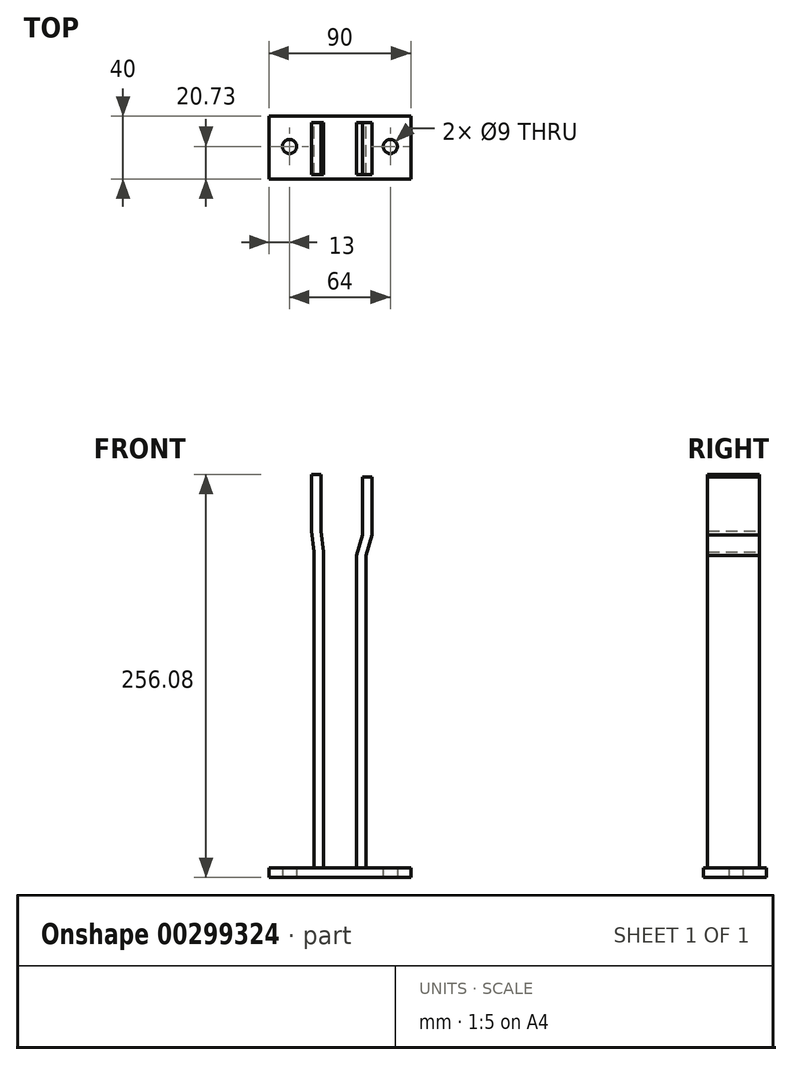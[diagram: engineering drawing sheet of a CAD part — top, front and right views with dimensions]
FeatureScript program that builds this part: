
annotation { "Feature Type Name" : "Feature", "Feature Type Description" : "" }
export const myFeature = defineFeature(function(context is Context, id is Id, definition is map)
    precondition{}
    {
        {
            var Q0;
            Q0=qCreatedBy(makeId("Right.planeOp"),FACE);
            var sketch = newSketch(context, id + "F0", { "sketchPlane" : qUnion([Q0])});
            skLineSegment(sketch, "E0.bottom", {"start": v(-20.73, 6) * mm, "end": v(19.27, 6) * mm});
            skLineSegment(sketch, "E0.left", {"start": v(-20.73, 6) * mm, "end": v(-20.73, 0) * mm});
            skLineSegment(sketch, "E0.right", {"start": v(19.27, 6) * mm, "end": v(19.27, 0) * mm});
            skLineSegment(sketch, "E1.trimOffspring", {"start": v(-20.73, 0) * mm, "end": v(19.27, 0) * mm});
            skSolve(sketch);
        }
        {
            var Q0;
            {var subQ3=sQuery(id+"F0.wireOp",EDGE,"ff7b447e-6627-4066-b775-27bb9192647b.left");Q0=makeQuery(id+"F0.imprint","IMPRINT",FACE,{"disambiguationData":[TD([[makeQuery(id+"F0.imprint","IMPRINT",EDGE,{"derivedFrom":subQ3}),-1.0]])]});}
            var Q1;
            {var subQ3=sQuery(id+"F0.wireOp",EDGE,"ff7b447e-6627-4066-b775-27bb9192647b.right");Q1=makeQuery(id+"F0.imprint","IMPRINT",FACE,{"disambiguationData":[TD([[makeQuery(id+"F0.imprint","IMPRINT",EDGE,{"derivedFrom":subQ3}),1.0]])]});}
            var Q2;
            {var subQ0=sQuery(id+"F0.wireOp",EDGE,"ff7b447e-6627-4066-b775-27bb9192647b.top");Q2=makeQuery(id+"F0.imprint","IMPRINT",FACE,{"disambiguationData":[TD([[makeQuery(id+"F0.imprint","IMPRINT",EDGE,{"derivedFrom":subQ0}),-1.0]])]});}
            var Q3;
            {var subQ5=sQuery(id+"F0.wireOp",EDGE,"E0.left");Q3=makeQuery(id+"F0.imprint","IMPRINT",FACE,{"disambiguationData":[TD([[makeQuery(id+"F0.imprint","IMPRINT",EDGE,{"derivedFrom":subQ5}),1.0]])]});}
            var Q4;
            {var subQ5=sQuery(id+"F0.wireOp",EDGE,"E0.right");Q4=makeQuery(id+"F0.imprint","IMPRINT",FACE,{"disambiguationData":[TD([[makeQuery(id+"F0.imprint","IMPRINT",EDGE,{"derivedFrom":subQ5}),-1.0]])]});}
            extrude(context, id + "F1", {"entities" : qUnion([Q0, Q1, Q2, Q3, Q4]), "depth" : 90 * mm});
        }
        {
            var Q0;
            Q0=qCreatedBy(makeId("Top.planeOp"),FACE);
            var sketch = newSketch(context, id + "F2", { "sketchPlane" : qUnion([Q0])});
            skLineSegment(sketch, "E2.bottom", {"start": v(28.5, 14.5) * mm, "end": v(34.5, 14.5) * mm});
            skLineSegment(sketch, "E2.top", {"start": v(28.5, -15.98) * mm, "end": v(34.5, -15.98) * mm});
            skLineSegment(sketch, "E2.left", {"start": v(28.5, 14.5) * mm, "end": v(28.5, -15.98) * mm});
            skLineSegment(sketch, "E2.right", {"start": v(34.5, 14.5) * mm, "end": v(34.5, -15.98) * mm});
            skLineSegment(sketch, "E3.bottom", {"start": v(55.5, 14.27) * mm, "end": v(61.5, 14.27) * mm});
            skLineSegment(sketch, "E3.top", {"start": v(55.5, -15.73) * mm, "end": v(61.5, -15.73) * mm});
            skLineSegment(sketch, "E3.left", {"start": v(55.5, 14.27) * mm, "end": v(55.5, -15.73) * mm});
            skLineSegment(sketch, "E3.right", {"start": v(61.5, 14.27) * mm, "end": v(61.5, -15.73) * mm});
            skLineSegment(sketch, "E4", {"start": v(0, -20.73) * mm, "end": v(90, -20.73) * mm, "construction": true});
            skLineSegment(sketch, "E5", {"start": v(90, 19.27) * mm, "end": v(90, -20.73) * mm, "construction": true});
            skPoint(sketch, "E6.center.orphan", {"position": v(77, 0) * mm});
            skPoint(sketch, "E7.center.orphan", {"position": v(13, 0) * mm});
            skSolve(sketch);
        }
        {
            var Q0;
            Q0=qCreatedBy(makeId("Top.planeOp"),FACE);
            var sketch = newSketch(context, id + "F3", { "sketchPlane" : qUnion([Q0])});
            skCircle(sketch, "E8", {"center": v(77, 0) * mm, "radius": 5 * mm});
            skCircle(sketch, "E9", {"center": v(13, 0) * mm, "radius": 5 * mm});
            skSolve(sketch);
        }
        {
            var Q0;
            Q0=sQuery(id+"F3.wireOp",VERTEX,"E9.center");
            var Q1;
            Q1=sQuery(id+"F3.wireOp",VERTEX,"E8.center");
            var Q2;
            Q2=makeQuery(id+"F1.opExtrude","SWEPT_BODY",BODY,{"disambiguationData":[OSD([sQuery(id+"F0.wireOp",EDGE,"E0.bottom"),sQuery(id+"F0.wireOp",EDGE,"E0.left"),sQuery(id+"F0.wireOp",EDGE,"E0.right"),sQuery(id+"F0.wireOp",EDGE,"E1.trimOffspring")])]});
            hole(context, id + "F4", {"style" : HoleStyle.SIMPLE, "endStyle" : HoleEndStyle.THROUGH, "oppositeDirection" : true, "holeDiameter" : 9 * mm, "tappedDepth" : 12 * mm, "tapClearance" : 3, "locations" : qUnion([Q0, Q1]), "scope" : qUnion([Q2])});
        }
        {
            var Q0;
            Q0=qCreatedBy(makeId("Front.planeOp"),FACE);
            var sketch = newSketch(context, id + "F5", { "sketchPlane" : qUnion([Q0])});
            skLineSegment(sketch, "E10.bottom", {"start": v(28.5, 206.79) * mm, "end": v(34.5, 206.79) * mm});
            skLineSegment(sketch, "E10.top", {"start": v(28.5, 0) * mm, "end": v(34.5, 0) * mm});
            skLineSegment(sketch, "E10.left", {"start": v(28.5, 206.79) * mm, "end": v(28.5, 0) * mm});
            skLineSegment(sketch, "E10.right", {"start": v(34.5, 206.79) * mm, "end": v(34.5, 0) * mm});
            skLineSegment(sketch, "E11.bottom", {"start": v(55.5, 204.63) * mm, "end": v(61.5, 204.63) * mm});
            skLineSegment(sketch, "E11.top", {"start": v(55.5, 0) * mm, "end": v(61.5, 0) * mm});
            skLineSegment(sketch, "E11.left", {"start": v(55.5, 204.63) * mm, "end": v(55.5, 0) * mm});
            skLineSegment(sketch, "E11.right", {"start": v(61.5, 204.63) * mm, "end": v(61.5, 0) * mm});
            skLineSegment(sketch, "E12.bottom", {"start": v(59.42, 217.5) * mm, "end": v(65.42, 217.5) * mm});
            skLineSegment(sketch, "E12.top", {"start": v(59.42, 254.49) * mm, "end": v(65.42, 254.49) * mm});
            skLineSegment(sketch, "E12.left", {"start": v(59.42, 217.5) * mm, "end": v(59.42, 254.49) * mm});
            skLineSegment(sketch, "E12.right", {"start": v(65.42, 217.5) * mm, "end": v(65.42, 254.49) * mm});
            skLineSegment(sketch, "E13.bottom", {"start": v(32.97, 219.9) * mm, "end": v(26.97, 219.9) * mm});
            skLineSegment(sketch, "E13.top", {"start": v(32.97, 256.08) * mm, "end": v(26.97, 256.08) * mm});
            skLineSegment(sketch, "E13.left", {"start": v(32.97, 219.9) * mm, "end": v(32.97, 256.08) * mm});
            skLineSegment(sketch, "E13.right", {"start": v(26.97, 219.9) * mm, "end": v(26.97, 256.08) * mm});
            skLineSegment(sketch, "E14", {"start": v(26.97, 219.9) * mm, "end": v(28.5, 206.79) * mm});
            skLineSegment(sketch, "E15", {"start": v(32.97, 219.9) * mm, "end": v(34.5, 206.79) * mm});
            skLineSegment(sketch, "E16", {"start": v(59.42, 217.5) * mm, "end": v(55.5, 204.63) * mm});
            skLineSegment(sketch, "E17", {"start": v(65.42, 217.5) * mm, "end": v(61.5, 204.63) * mm});
            skSolve(sketch);
        }
        {
            var Q0;
            Q0=makeQuery(id+"F5.imprint","IMPRINT",FACE,{"disambiguationData":[TD([[makeQuery(id+"F5.imprint","IMPRINT",EDGE,{"derivedFrom":sQuery(id+"F5.wireOp",EDGE,"E12.bottom")}),1.0]])]});
            var Q1;
            Q1=makeQuery(id+"F5.imprint","IMPRINT",FACE,{"disambiguationData":[TD([[makeQuery(id+"F5.imprint","IMPRINT",EDGE,{"derivedFrom":sQuery(id+"F5.wireOp",EDGE,"E11.bottom")}),1.0]])]});
            var Q2;
            Q2=makeQuery(id+"F5.imprint","IMPRINT",FACE,{"disambiguationData":[TD([[makeQuery(id+"F5.imprint","IMPRINT",EDGE,{"derivedFrom":sQuery(id+"F5.wireOp",EDGE,"E11.bottom")}),-1.0]])]});
            var Q3;
            Q3=makeQuery(id+"F5.imprint","IMPRINT",FACE,{"disambiguationData":[TD([[makeQuery(id+"F5.imprint","IMPRINT",EDGE,{"derivedFrom":sQuery(id+"F5.wireOp",EDGE,"E10.bottom")}),-1.0]])]});
            var Q4;
            Q4=makeQuery(id+"F5.imprint","IMPRINT",FACE,{"disambiguationData":[TD([[makeQuery(id+"F5.imprint","IMPRINT",EDGE,{"derivedFrom":sQuery(id+"F5.wireOp",EDGE,"E10.bottom")}),1.0]])]});
            var Q5;
            Q5=makeQuery(id+"F5.imprint","IMPRINT",FACE,{"disambiguationData":[TD([[makeQuery(id+"F5.imprint","IMPRINT",EDGE,{"derivedFrom":sQuery(id+"F5.wireOp",EDGE,"E13.bottom")}),-1.0]])]});
            extrude(context, id + "F6", {"entities" : qUnion([Q0, Q1, Q2, Q3, Q4, Q5]), "operationType" : NewBodyOperationType.ADD, "depth" : 18 * mm});
        }
        {
            var Q0;
            Q0=makeQuery(id+"F6.opExtrude","CAP_FACE",FACE,{"disambiguationData":[OSD([sQuery(id+"F5.wireOp",EDGE,"E10.top"),sQuery(id+"F5.wireOp",EDGE,"E10.left"),sQuery(id+"F5.wireOp",EDGE,"E10.right"),sQuery(id+"F5.wireOp",EDGE,"E13.top"),sQuery(id+"F5.wireOp",EDGE,"E13.left"),sQuery(id+"F5.wireOp",EDGE,"E13.right"),sQuery(id+"F5.wireOp",EDGE,"E14"),sQuery(id+"F5.wireOp",EDGE,"E15")])],"isStart":true});
            var Q1;
            Q1=makeQuery(id+"F6.opExtrude","CAP_FACE",FACE,{"disambiguationData":[OSD([sQuery(id+"F5.wireOp",EDGE,"E11.top"),sQuery(id+"F5.wireOp",EDGE,"E11.left"),sQuery(id+"F5.wireOp",EDGE,"E11.right"),sQuery(id+"F5.wireOp",EDGE,"E12.top"),sQuery(id+"F5.wireOp",EDGE,"E12.left"),sQuery(id+"F5.wireOp",EDGE,"E12.right"),sQuery(id+"F5.wireOp",EDGE,"E16"),sQuery(id+"F5.wireOp",EDGE,"E17")])],"isStart":true});
            extrude(context, id + "F7", {"entities" : qUnion([Q0, Q1]), "operationType" : NewBodyOperationType.ADD, "depth" : 15 * mm});
        }
    });
